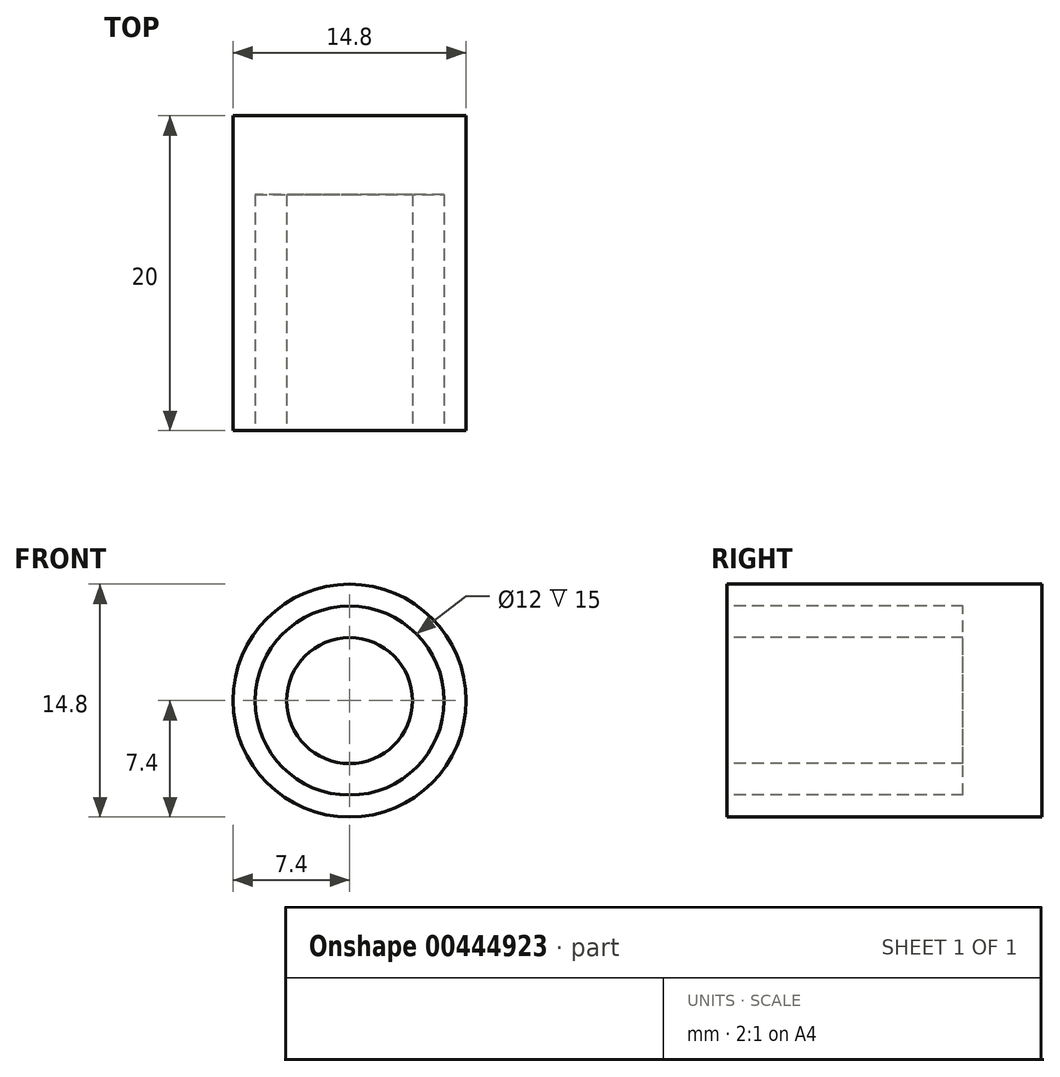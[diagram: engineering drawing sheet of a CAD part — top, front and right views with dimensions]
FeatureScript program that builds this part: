
annotation { "Feature Type Name" : "Feature", "Feature Type Description" : "" }
export const myFeature = defineFeature(function(context is Context, id is Id, definition is map)
    precondition{}
    {
        {
            var Q0;
            Q0=qCreatedBy(makeId("Front.planeOp"),FACE);
            var sketch = newSketch(context, id + "F0", { "sketchPlane" : qUnion([Q0])});
            skCircle(sketch, "E0", {"center": v(0, 0) * mm, "radius": 7.4 * mm});
            skSolve(sketch);
        }
        {
            var Q0;
            Q0 = qSketchRegion(id + "F0", true);
            extrude(context, id + "F1", {"entities" : qUnion([Q0]), "oppositeDirection" : true, "depth" : 20 * mm});
        }
        {
            var Q0;
            Q0=makeQuery(id+"F1.opExtrude","CAP_FACE",FACE,{"disambiguationData":[OSD([sQuery(id+"F0.wireOp",EDGE,"E0")])],"isStart":true});
            var sketch = newSketch(context, id + "F2", { "sketchPlane" : qUnion([Q0])});
            skCircle(sketch, "E1", {"center": v(0, 0) * mm, "radius": 4 * mm});
            skCircle(sketch, "E2", {"center": v(0, 0) * mm, "radius": 6 * mm});
            skSolve(sketch);
        }
        {
            var Q0;
            Q0=makeQuery(id+"F2.imprint","IMPRINT",FACE,{"disambiguationData":[TD([[makeQuery(id+"F2.imprint","IMPRINT",EDGE,{"derivedFrom":sQuery(id+"F2.wireOp",EDGE,"E1")}),-1.0]])]});
            extrude(context, id + "F3", {"entities" : qUnion([Q0]), "operationType" : NewBodyOperationType.REMOVE, "oppositeDirection" : true, "depth" : 15 * mm});
        }
    });
